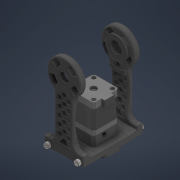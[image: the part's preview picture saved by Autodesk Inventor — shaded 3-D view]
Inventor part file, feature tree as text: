
AUTODESK INVENTOR PART (.ipt)
format: ipt  version: 2022 (Build 260153070, 153G)  size: 4,290,048 bytes
history: native  units: mm
features: other x31, projected_geometry x4, extrude x1, sketch x1
ambient origin geometry x8: Origin, YZ Plane, XZ Plane, XY Plane, X Axis, Y Axis, Z Axis, Center Point
bodies: Solid1 (feature_tree)
feature tree (37):
  other  "long_link.iam"
  other  "Stepper_nema17.ipt:1"
  other  "reductor_topless.iam:1::Stator_encoder_lite.ipt:1"
  other  "reductor_topless.iam:1::Center_encoder_lite.ipt:1"
  other  "reductor_topless.iam:1::Excenter_lite.ipt:1"
  other  "reductor_topless.iam:1::Stator_lite.ipt:1"
  other  "reductor_topless.iam:1::Disk_lite.ipt:1"
  other  "reductor_topless.iam:1::DIN 625 - T1 619/8 - 8 x 19 x 6:1"
  other  "reductor_topless.iam:1::Center_lite.ipt:1"
  other  "reductor_topless.iam:1::DIN 625 - T1 619/8 - 8 x 19 x 6:2"
  other  "reductor_topless.iam:1::Rotor_lite.ipt:1"
  other  "reductor_topless.iam:1::Board.ipt:1"
  other  "reductor_topless.iam:1::Magnet.ipt:1"
  other  "Stepper_holder_2_lite.ipt:1"
  other  "Forearm_long_1.ipt:1"
  other  "Forearm_long_2.ipt:1"
  other  "Limit_switch.ipt:1"
  other  "DIN 912 - replaced by DIN EN ISO 4762 M2.5 x 4:1"
  other  "DIN 912 - replaced by DIN EN ISO 4762 M2.5 x 4:2"
  other  "DIN 912 - replaced by DIN EN ISO 4762 M5 x 16:3"
  other  "DIN 912 - replaced by DIN EN ISO 4762 M5 x 16:4"
  other  "DIN 912 - replaced by DIN EN ISO 4762 M5 x 16:2"
  other  "DIN 912 - replaced by DIN EN ISO 4762 M5 x 16:1"
  other  "DIN 912 - replaced by DIN EN ISO 4762 M4 x 25:3"
  other  "DIN 912 - replaced by DIN EN ISO 4762 M4 x 25:4"
  other  "DIN 912 - replaced by DIN EN ISO 4762 M4 x 25:2"
  other  "DIN 912 - replaced by DIN EN ISO 4762 M4 x 25:1"
  other  "DIN 912 - replaced by DIN EN ISO 4762 M4 x 16:2"
  other  "DIN 912 - replaced by DIN EN ISO 4762 M4 x 16:1"
  other  "DIN 912 - replaced by DIN EN ISO 4762 M4 x 16:3"
  other  "DIN 912 - replaced by DIN EN ISO 4762 M4 x 16:4"
  extrude  "Extrusion1"  Depth=10.0mm TaperAngle=0.0deg
  sketch  "Sketch1"  dims[d0=10.0mm d1=10.0mm d2=0.0mm]
  projected_geometry  "Projected Loop1"
  projected_geometry  "Projected Loop2"
  projected_geometry  "Projected Loop3"
  projected_geometry  "Projected Loop4"
